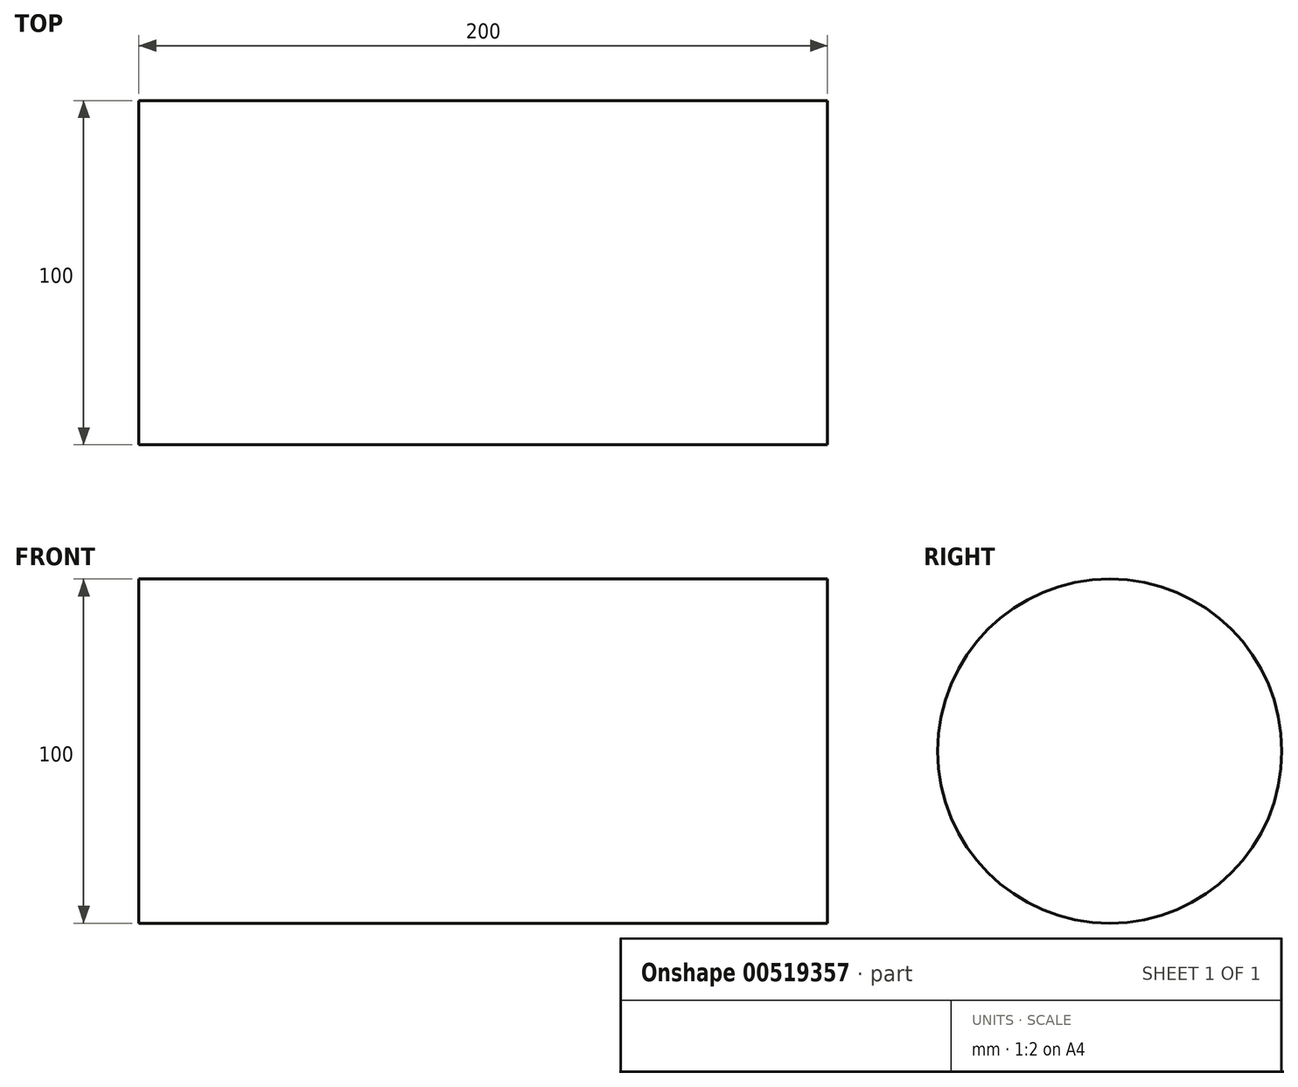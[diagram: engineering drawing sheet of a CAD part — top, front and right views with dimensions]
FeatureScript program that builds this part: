
annotation { "Feature Type Name" : "Feature", "Feature Type Description" : "" }
export const myFeature = defineFeature(function(context is Context, id is Id, definition is map)
    precondition{}
    {
        {
            var Q0;
            Q0=qCreatedBy(makeId("Front.planeOp"),FACE);
            var sketch = newSketch(context, id + "F0", { "sketchPlane" : qUnion([Q0])});
            skLineSegment(sketch, "E0.bottom", {"start": v(-100, 25) * mm, "end": v(100, 25) * mm});
            skLineSegment(sketch, "E0.top", {"start": v(-100, -25) * mm, "end": v(100, -25) * mm});
            skLineSegment(sketch, "E0.left", {"start": v(-100, 25) * mm, "end": v(-100, -25) * mm});
            skLineSegment(sketch, "E0.right", {"start": v(100, 25) * mm, "end": v(100, -25) * mm});
            skPoint(sketch, "E0.middle", {"position": v(0, 0) * mm});
            skSolve(sketch);
        }
        {
            var Q0;
            Q0=makeQuery(id+"F0.imprint","IMPRINT",FACE,{"disambiguationData":[TD([[makeQuery(id+"F0.imprint","IMPRINT",EDGE,{"derivedFrom":sQuery(id+"F0.wireOp",EDGE,"E0.bottom")}),-1.0]])]});
            var Q1;
            Q1=sQuery(id+"F0.wireOp",EDGE,"E0.bottom");
            revolve(context, id + "F1", {"entities" : qUnion([Q0]), "axis" : qUnion([Q1]), "revolveType" : RevolveType.FULL});
        }
    });
